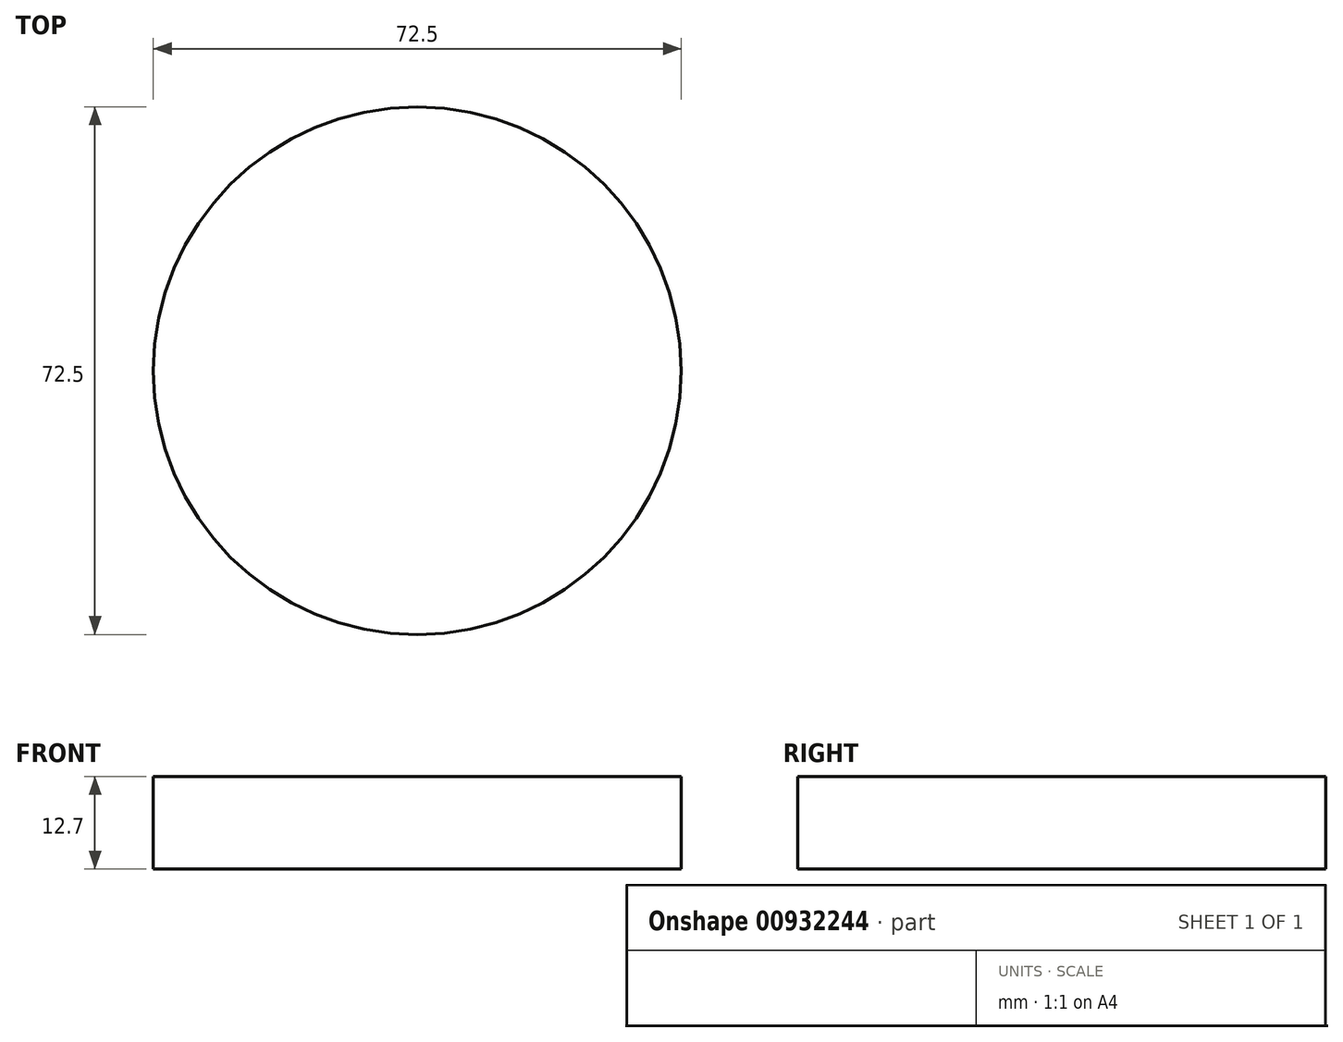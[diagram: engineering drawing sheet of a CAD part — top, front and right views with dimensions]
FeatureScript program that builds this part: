
annotation { "Feature Type Name" : "Feature", "Feature Type Description" : "" }
export const myFeature = defineFeature(function(context is Context, id is Id, definition is map)
    precondition{}
    {
        {
            var Q0;
            Q0=qCreatedBy(makeId("Top.planeOp"),FACE);
            var sketch = newSketch(context, id + "F0", { "sketchPlane" : qUnion([Q0])});
            skCircle(sketch, "E0", {"center": v(0, 0) * mm, "radius": 36.25 * mm});
            skSolve(sketch);
        }
        {
            var Q0;
            Q0=makeQuery(id+"F0.imprint","IMPRINT",FACE,{"disambiguationData":[TD([[makeQuery(id+"F0.imprint","IMPRINT",EDGE,{"derivedFrom":sQuery(id+"F0.wireOp",EDGE,"E0")}),1.0]])]});
            extrude(context, id + "F1", {"entities" : qUnion([Q0]), "depth" : 12.7 * mm, "offsetDistance" : 25 * mm});
        }
    });
